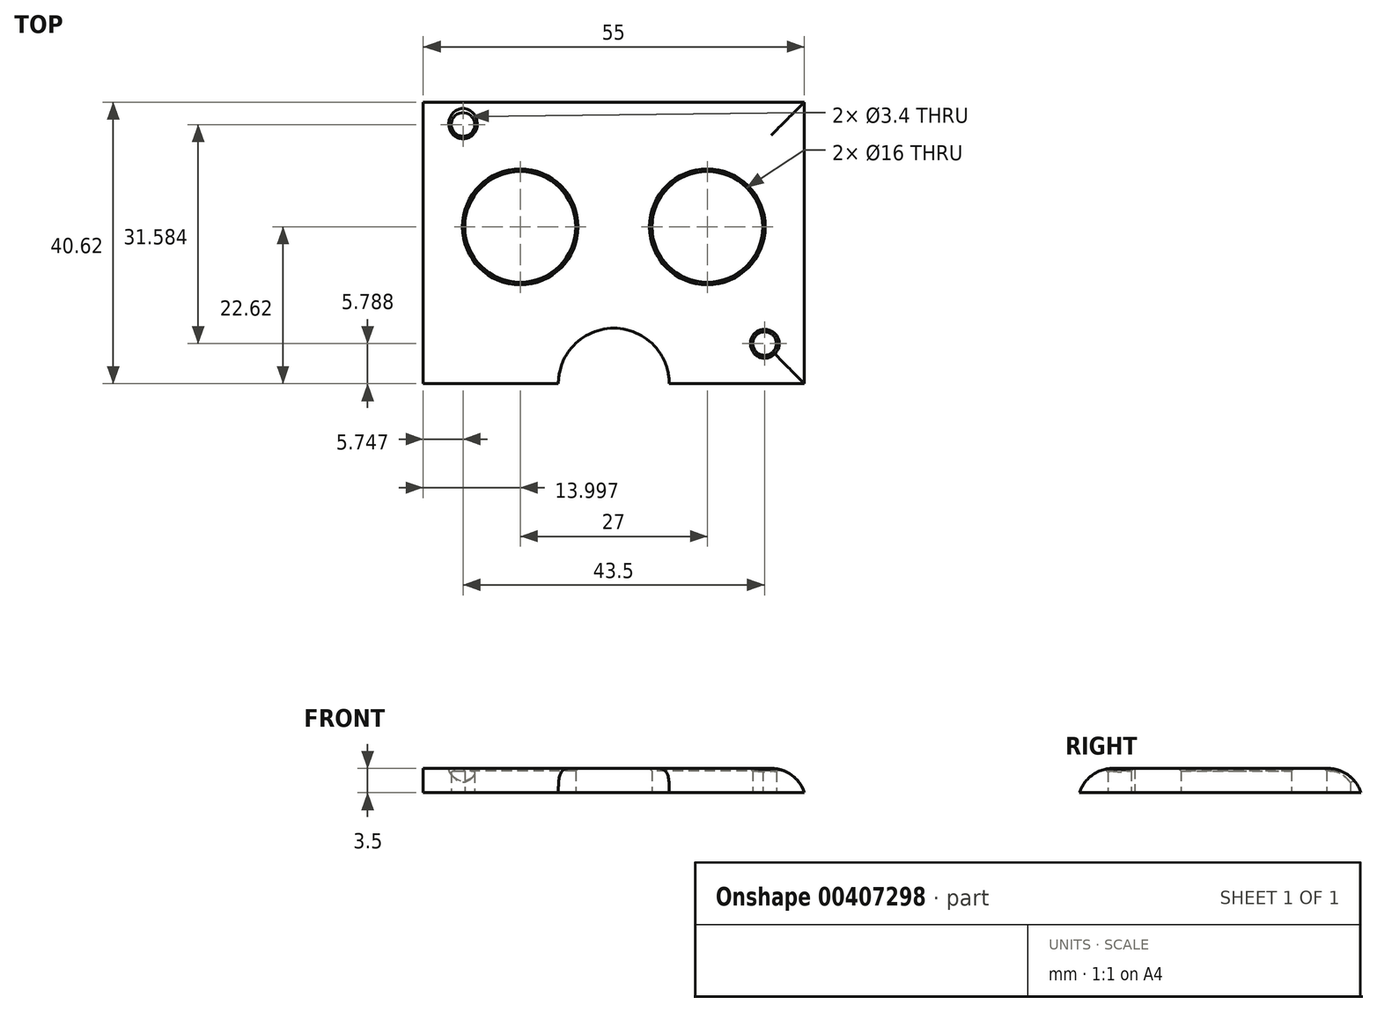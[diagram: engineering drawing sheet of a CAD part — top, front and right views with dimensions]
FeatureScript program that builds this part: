
annotation { "Feature Type Name" : "Feature", "Feature Type Description" : "" }
export const myFeature = defineFeature(function(context is Context, id is Id, definition is map)
    precondition{}
    {
        {
            var Q0;
            Q0=qCreatedBy(makeId("Top.planeOp"),FACE);
            var sketch = newSketch(context, id + "F0", { "sketchPlane" : qUnion([Q0])});
            skLineSegment(sketch, "E0", {"start": v(-26.05, -21.32) * mm, "end": v(-26.05, 19.3) * mm});
            skLineSegment(sketch, "E1.bottom", {"start": v(-23.55, 19.3) * mm, "end": v(-17.05, 19.3) * mm});
            skLineSegment(sketch, "E1.top", {"start": v(-23.55, 12.8) * mm, "end": v(-17.05, 12.8) * mm});
            skLineSegment(sketch, "E1.left", {"start": v(-23.55, 19.3) * mm, "end": v(-23.55, 12.8) * mm});
            skLineSegment(sketch, "E1.right", {"start": v(-17.05, 19.3) * mm, "end": v(-17.05, 12.8) * mm});
            skCircle(sketch, "E2", {"center": v(-20.3, 16.05) * mm, "radius": 1.7 * mm});
            skPoint(sketch, "E2.centerSnap0", {"position": v(-19.55, 16.05) * mm});
            skPoint(sketch, "E2.centerSnap1", {"position": v(-22.8, 19.3) * mm});
            skLineSegment(sketch, "E3.bottom", {"start": v(26.45, -18.78) * mm, "end": v(19.95, -18.78) * mm});
            skLineSegment(sketch, "E3.top", {"start": v(26.45, -12.28) * mm, "end": v(19.95, -12.28) * mm});
            skLineSegment(sketch, "E3.left", {"start": v(26.45, -18.78) * mm, "end": v(26.45, -12.28) * mm});
            skLineSegment(sketch, "E3.right", {"start": v(19.95, -18.78) * mm, "end": v(19.95, -12.28) * mm});
            skCircle(sketch, "E4", {"center": v(23.2, -15.53) * mm, "radius": 1.7 * mm});
            skPoint(sketch, "E4.centerSnap0", {"position": v(22.45, -18.07) * mm});
            skPoint(sketch, "E4.centerSnap1", {"position": v(25.7, -14.82) * mm});
            skLineSegment(sketch, "E5.bottom", {"start": v(-26.05, -21.32) * mm, "end": v(28.95, -21.32) * mm});
            skLineSegment(sketch, "E5.top", {"start": v(-26.05, 19.3) * mm, "end": v(28.95, 19.3) * mm});
            skLineSegment(sketch, "E5.right", {"start": v(28.95, -21.32) * mm, "end": v(28.95, 19.3) * mm});
            skLineSegment(sketch, "E6", {"start": v(0, -15.53) * mm, "end": v(0, -10.66) * mm});
            skPoint(sketch, "E7.endSnap0", {"position": v(19.95, -15.53) * mm});
            skLineSegment(sketch, "E8", {"start": v(23.2, -15.53) * mm, "end": v(8.68, -15.53) * mm});
            skLineSegment(sketch, "E9", {"start": v(28.95, -21.32) * mm, "end": v(1.45, -21.32) * mm});
            skLineSegment(sketch, "E10", {"start": v(1.45, -21.32) * mm, "end": v(1.45, -10.66) * mm});
            skLineSegment(sketch, "E11", {"start": v(1.45, -10.66) * mm, "end": v(1.45, -0.66) * mm});
            skLineSegment(sketch, "E12", {"start": v(1.45, 1.3) * mm, "end": v(14.95, 1.3) * mm});
            skLineSegment(sketch, "E13.MirrorCS", {"start": v(1.45, 1.3) * mm, "end": v(-12.05, 1.3) * mm});
            skCircle(sketch, "E14", {"center": v(-12.05, 1.3) * mm, "radius": 8 * mm});
            skCircle(sketch, "E15", {"center": v(14.95, 1.3) * mm, "radius": 8 * mm});
            skCircle(sketch, "E16", {"center": v(1.45, -21.32) * mm, "radius": 8 * mm});
            skSolve(sketch);
        }
        {
            var Q0;
            Q0=makeQuery(id+"F0.imprint","IMPRINT",FACE,{"disambiguationData":[TD([[makeQuery(id+"F0.imprint","IMPRINT",EDGE,{"derivedFrom":sQuery(id+"F0.wireOp",EDGE,"E1.top")}),-1.0]])]});
            var Q1;
            Q1=makeQuery(id+"F0.imprint","IMPRINT",FACE,{"disambiguationData":[TD([[makeQuery(id+"F0.imprint","IMPRINT",EDGE,{"derivedFrom":sQuery(id+"F0.wireOp",EDGE,"E1.top")}),1.0]])]});
            var Q2;
            {var subQ1=sQuery(id+"F0.wireOp",EDGE,"E3.bottom");Q2=makeQuery(id+"F0.imprint","IMPRINT",FACE,{"disambiguationData":[TD([[makeQuery(id+"F0.imprint","IMPRINT",EDGE,{"derivedFrom":subQ1}),-1.0]])]});}
            extrude(context, id + "F1", {"entities" : qUnion([Q0, Q1, Q2]), "depth" : 3.5 * mm});
        }
        {
            var Q0;
            Q0=makeQuery(id+"F1.opExtrude","CAP_EDGE",EDGE,{"disambiguationData":[OSD([sQuery(id+"F0.wireOp",EDGE,"E0")])],"isStart":false});
            var Q1;
            Q1=makeQuery(id+"F1.opExtrude","CAP_EDGE",EDGE,{"disambiguationData":[OSD([sQuery(id+"F0.wireOp",EDGE,"E5.bottom"),sQuery(id+"F0.wireOp",EDGE,"E9")])],"isStart":false});
            var Q2;
            Q2=makeQuery(id+"F1.opExtrude","CAP_EDGE",EDGE,{"disambiguationData":[OSD([sQuery(id+"F0.wireOp",EDGE,"E5.right")])],"isStart":false});
            var Q3;
            Q3=makeQuery(id+"F1.opExtrude","CAP_EDGE",EDGE,{"disambiguationData":[OSD([sQuery(id+"F0.wireOp",EDGE,"E5.top")])],"isStart":false});
            fillet(context, id + "F2", {"entities" : qUnion([Q0, Q1, Q2, Q3]), "radius" : 5 * mm, "tangentPropagation" : true, "allowEdgeOverflow" : false});
        }
        {
            var Q0;
            Q0=makeQuery(id+"F2.opFillet","BLEND_EDGE",EDGE,{"blendedFrom":[makeQuery(id+"F1.opExtrude","CAP_EDGE",EDGE,{"disambiguationData":[OSD([sQuery(id+"F0.wireOp",EDGE,"E5.top")])],"isStart":false}),makeQuery(id+"F1.opExtrude","SWEPT_FACE",FACE,{"disambiguationData":[OSD([sQuery(id+"F0.wireOp",EDGE,"E2")])]})],"blendedInto":[makeQuery(id+"F1.opExtrude","SWEPT_FACE",FACE,{"disambiguationData":[OSD([sQuery(id+"F0.wireOp",EDGE,"E2")])]})]});
            var Q1;
            Q1=makeQuery(id+"F1.opExtrude","CAP_EDGE",EDGE,{"disambiguationData":[OSD([sQuery(id+"F0.wireOp",EDGE,"E2")])],"isStart":false});
            var Q2;
            Q2=makeQuery(id+"F1.opExtrude","CAP_EDGE",EDGE,{"disambiguationData":[OSD([sQuery(id+"F0.wireOp",EDGE,"E14")])],"isStart":false});
            var Q3;
            Q3=makeQuery(id+"F1.opExtrude","CAP_EDGE",EDGE,{"disambiguationData":[OSD([sQuery(id+"F0.wireOp",EDGE,"E15")])],"isStart":false});
            var Q4;
            Q4=makeQuery(id+"F1.opExtrude","CAP_EDGE",EDGE,{"disambiguationData":[OSD([sQuery(id+"F0.wireOp",EDGE,"E4")])],"isStart":false});
            var Q5;
            Q5=makeQuery(id+"F2.opFillet","BLEND_EDGE",EDGE,{"blendedFrom":[makeQuery(id+"F1.opExtrude","CAP_EDGE",EDGE,{"disambiguationData":[OSD([sQuery(id+"F0.wireOp",EDGE,"E5.right")])],"isStart":false}),makeQuery(id+"F1.opExtrude","SWEPT_FACE",FACE,{"disambiguationData":[OSD([sQuery(id+"F0.wireOp",EDGE,"E4")])]})],"blendedInto":[makeQuery(id+"F1.opExtrude","SWEPT_FACE",FACE,{"disambiguationData":[OSD([sQuery(id+"F0.wireOp",EDGE,"E4")])]})]});
            chamfer(context, id + "F3", {"entities" : qUnion([Q0, Q1, Q2, Q3, Q4, Q5]), "width" : 0.35 * mm, "tangentPropagation" : true});
        }
    });
